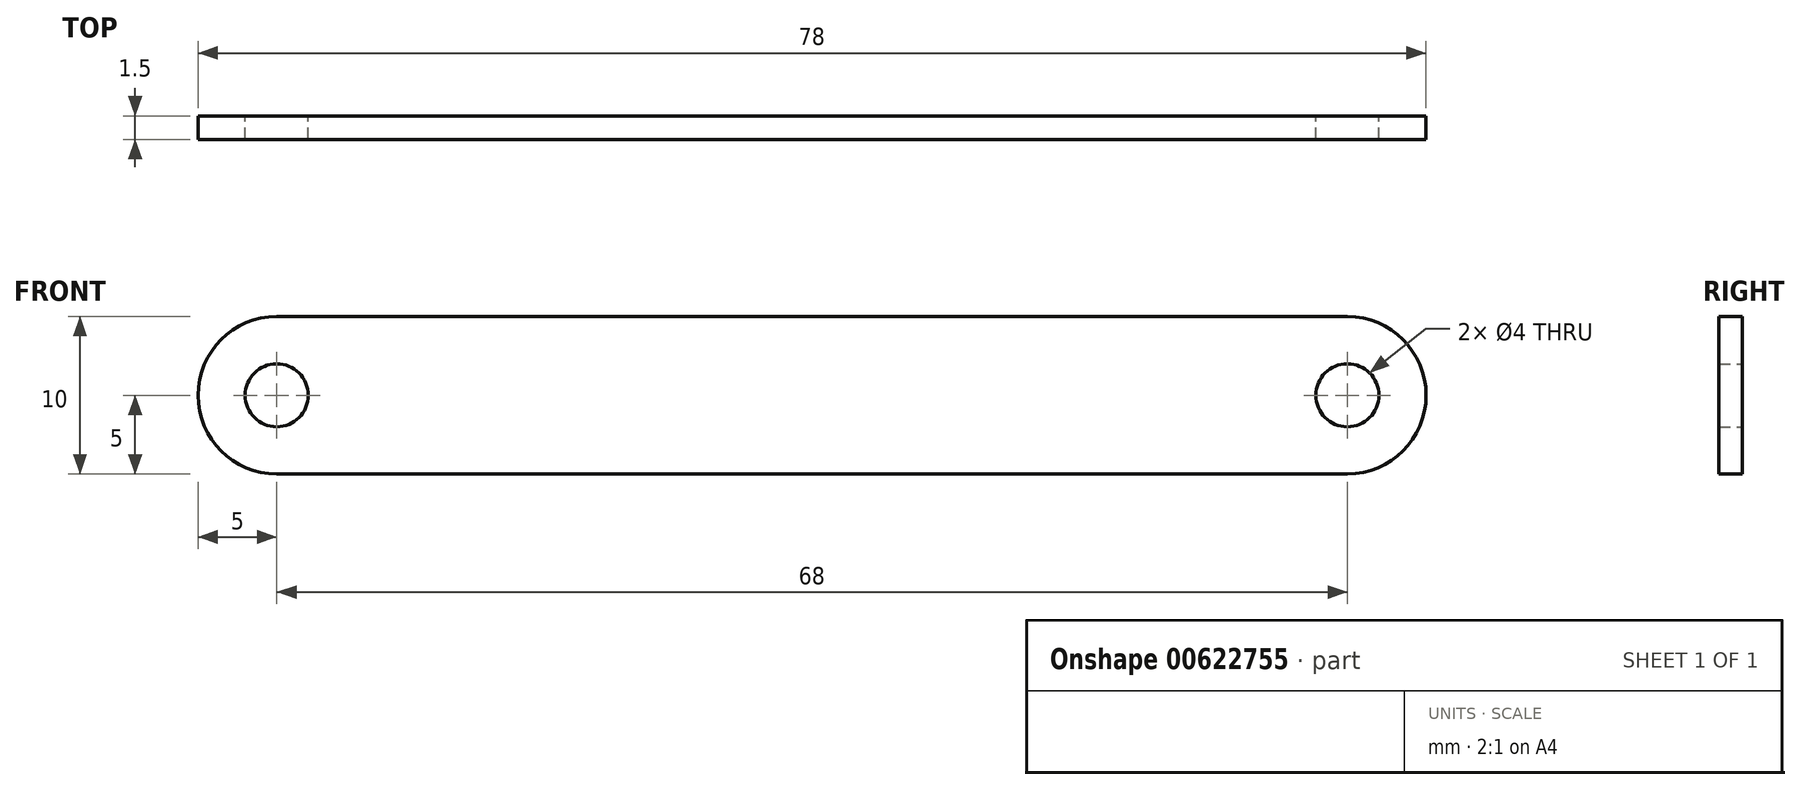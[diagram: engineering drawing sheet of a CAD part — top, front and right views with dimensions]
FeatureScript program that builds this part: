
annotation { "Feature Type Name" : "Feature", "Feature Type Description" : "" }
export const myFeature = defineFeature(function(context is Context, id is Id, definition is map)
    precondition{}
    {
        {
            var Q0;
            Q0=qCreatedBy(makeId("Front.planeOp"),FACE);
            var sketch = newSketch(context, id + "F0", { "sketchPlane" : qUnion([Q0])});
            skLineSegment(sketch, "E0.bottom", {"start": v(5, 0) * mm, "end": v(73, 0) * mm});
            skLineSegment(sketch, "E0.top", {"start": v(5, 10) * mm, "end": v(73, 10) * mm});
            skLineSegment(sketch, "E0.left", {"start": v(0, 5) * mm, "end": v(0, 5) * mm});
            skLineSegment(sketch, "E0.right", {"start": v(78, 5) * mm, "end": v(78, 5) * mm});
            skCircle(sketch, "E1", {"center": v(5, 5) * mm, "radius": 2 * mm});
            skCircle(sketch, "E2", {"center": v(73, 5) * mm, "radius": 2 * mm});
            skPoint(sketch, "E3.visualSharp", {"position": v(0, 10) * mm});
            skArc(sketch, "E3.filletArc", {"start": v(5, 10) * mm, "mid": v(1.46, 8.54) * mm, "end": v(0, 5) * mm});
            skPoint(sketch, "E4.visualSharp", {"position": v(0, 0) * mm});
            skArc(sketch, "E4.filletArc", {"start": v(0, 5) * mm, "mid": v(1.46, 1.46) * mm, "end": v(5, 0) * mm});
            skPoint(sketch, "E5.visualSharp", {"position": v(78, 10) * mm});
            skArc(sketch, "E5.filletArc", {"start": v(78, 5) * mm, "mid": v(76.54, 8.54) * mm, "end": v(73, 10) * mm});
            skPoint(sketch, "E6.visualSharp", {"position": v(78, 0) * mm});
            skArc(sketch, "E6.filletArc", {"start": v(73, 0) * mm, "mid": v(76.54, 1.46) * mm, "end": v(78, 5) * mm});
            skSolve(sketch);
        }
        {
            var Q0;
            Q0=makeQuery(id+"F0.imprint","IMPRINT",FACE,{"disambiguationData":[TD([[makeQuery(id+"F0.imprint","IMPRINT",EDGE,{"derivedFrom":sQuery(id+"F0.wireOp",EDGE,"E0.bottom")}),1.0]])]});
            extrude(context, id + "F1", {"entities" : qUnion([Q0]), "depth" : 1.5 * mm, "offsetDistance" : 25.4 * mm});
        }
    });
